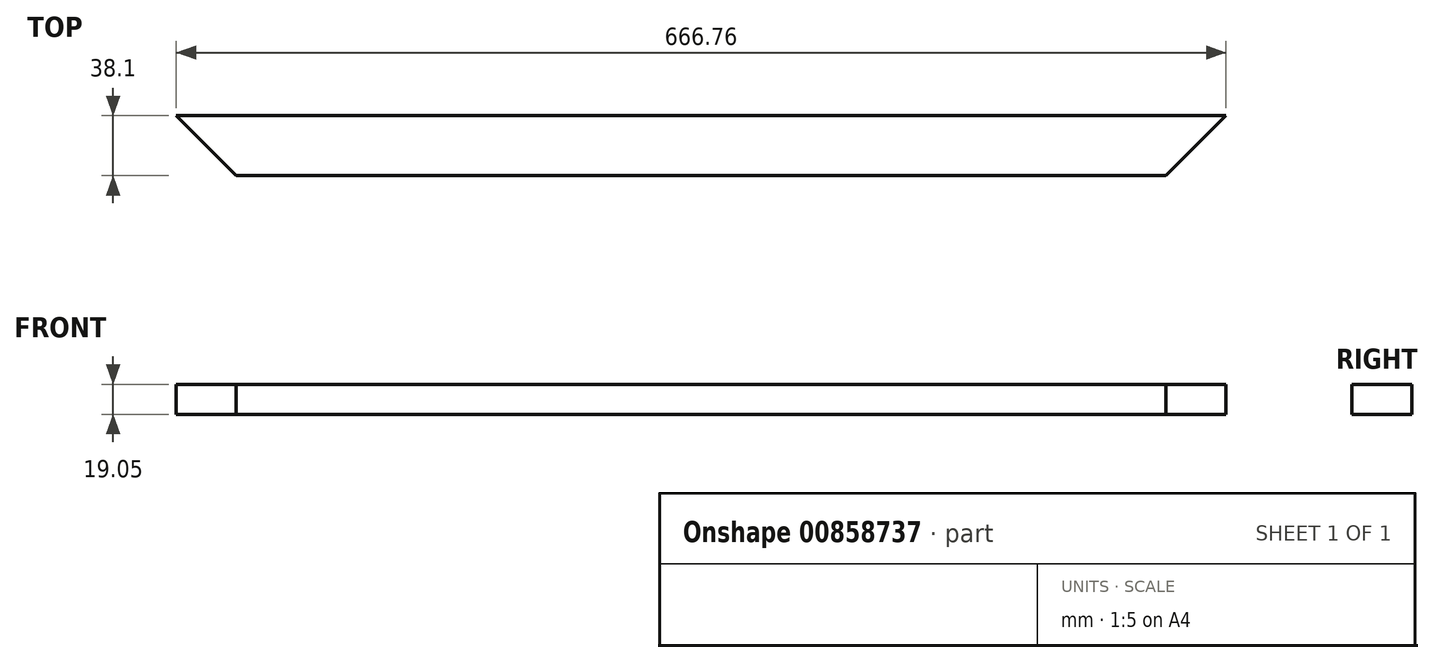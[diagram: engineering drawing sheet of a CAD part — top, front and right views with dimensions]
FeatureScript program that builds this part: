
annotation { "Feature Type Name" : "Feature", "Feature Type Description" : "" }
export const myFeature = defineFeature(function(context is Context, id is Id, definition is map)
    precondition{}
    {
        {
            var Q0;
            Q0=qCreatedBy(makeId("Top.planeOp"),FACE);
            var sketch = newSketch(context, id + "F0", { "sketchPlane" : qUnion([Q0])});
            skLineSegment(sketch, "E0.bottom", {"start": v(333.38, 19.05) * mm, "end": v(-333.38, 19.05) * mm});
            skLineSegment(sketch, "E0.top", {"start": v(333.38, -19.05) * mm, "end": v(-333.38, -19.05) * mm});
            skLineSegment(sketch, "E0.left", {"start": v(333.38, 19.05) * mm, "end": v(333.38, -19.05) * mm});
            skLineSegment(sketch, "E0.right", {"start": v(-333.38, 19.05) * mm, "end": v(-333.38, -19.05) * mm});
            skPoint(sketch, "E0.middle", {"position": v(0, 0) * mm});
            skSolve(sketch);
        }
        {
            var Q0;
            Q0=qSketchRegion(id+"F0",true);
            extrude(context, id + "F1", {"entities" : qUnion([Q0]), "depth" : 19.05 * mm, "offsetDistance" : 25.4 * mm});
        }
        {
            var Q0;
            Q0=makeQuery(id+"F1.opExtrude","SWEPT_EDGE",EDGE,{"disambiguationData":[OSD([sQuery(id+"F0.wireOp",EDGE,"E0.top"),sQuery(id+"F0.wireOp",EDGE,"E0.left")])]});
            var Q1;
            Q1=makeQuery(id+"F1.opExtrude","SWEPT_EDGE",EDGE,{"disambiguationData":[OSD([sQuery(id+"F0.wireOp",EDGE,"E0.top"),sQuery(id+"F0.wireOp",EDGE,"E0.right")])]});
            chamfer(context, id + "F2", {"entities" : qUnion([Q0, Q1]), "width" : 38.1 * mm, "tangentPropagation" : true});
        }
    });
